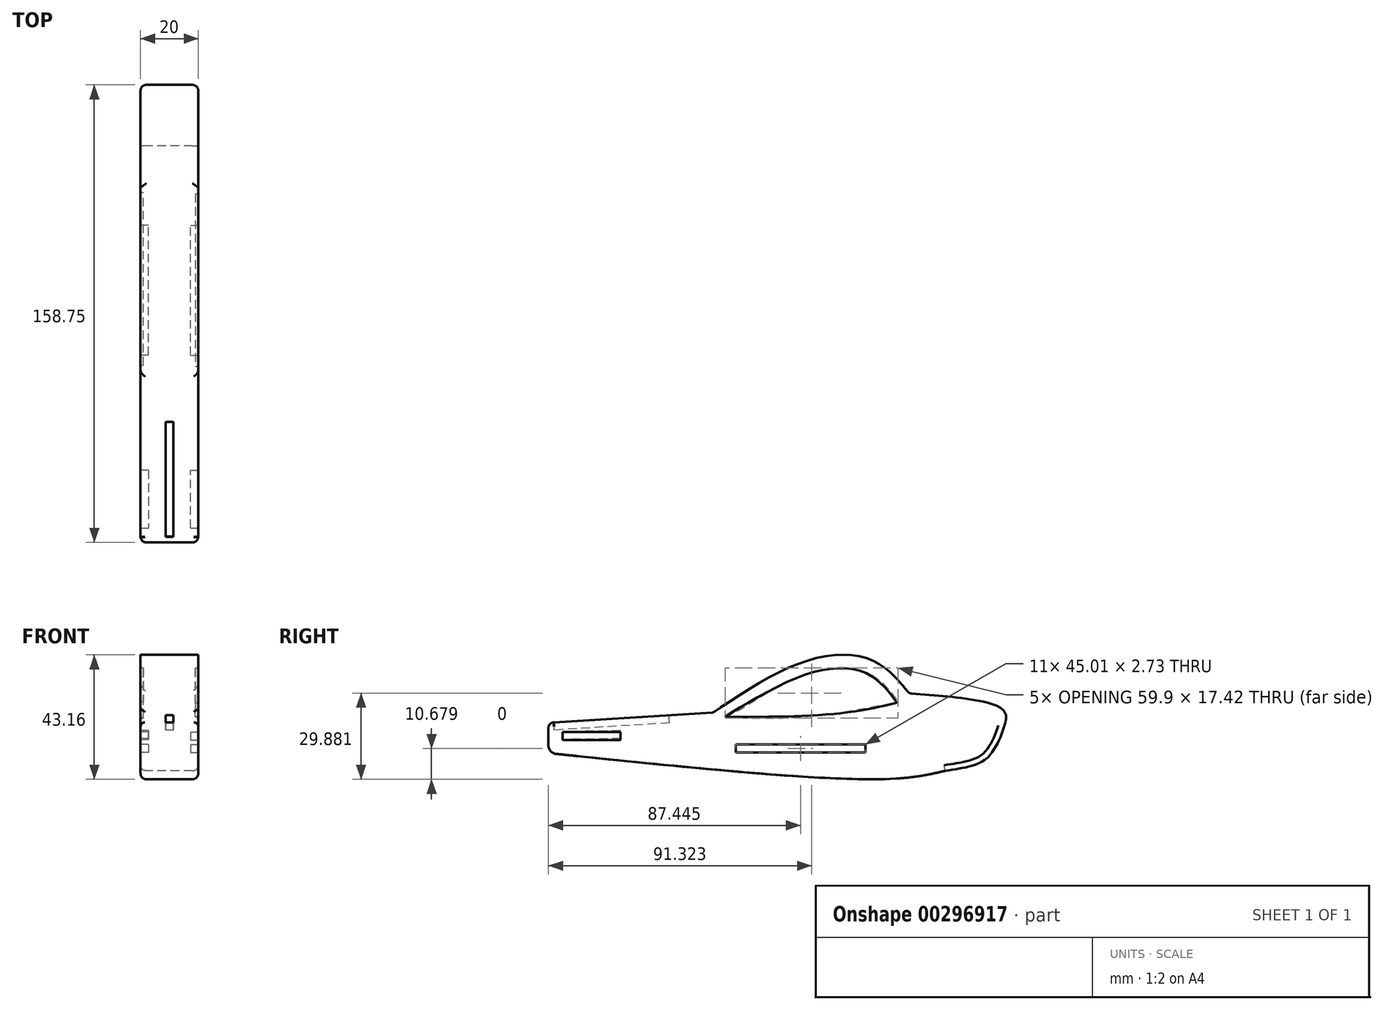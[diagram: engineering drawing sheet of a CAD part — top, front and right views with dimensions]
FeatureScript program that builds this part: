
annotation { "Feature Type Name" : "Feature", "Feature Type Description" : "" }
export const myFeature = defineFeature(function(context is Context, id is Id, definition is map)
    precondition{}
    {
        {
            var Q0;
            Q0=qCreatedBy(makeId("Right.planeOp"),FACE);
            var sketch = newSketch(context, id + "F0", { "sketchPlane" : qUnion([Q0])});
            skPoint(sketch, "E0.MirrorCS.end.orphan", {"position": v(-80.31, 27.96) * mm});
            skPoint(sketch, "E0.MirrorCS.start.orphan", {"position": v(0, 27.96) * mm});
            skFitSpline(sketch, "E1", {"points": [v(80.31, 27.96) * mm, v(77.68, 15.16) * mm, v(74.67, 8.15) * mm, v(70, 3.14) * mm, v(57.32, 0) * mm], "startDerivative": vector(-8.17, -48.04) * mm, "endDerivative": vector(-50.28, -7.34) * mm});
            skFitSpline(sketch, "E2", {"points": [v(57.32, 0) * mm, v(36.63, -2.86) * mm, v(-80.31, 6.15) * mm], "startDerivative": vector(-55.4, -12.98) * mm, "endDerivative": vector(-200.25, 20.71) * mm});
            skPoint(sketch, "E3.orphan", {"position": v(0, 0) * mm});
            skPoint(sketch, "E4.MirrorCS.end.orphan", {"position": v(-80.31, 0) * mm});
            skLineSegment(sketch, "E5", {"start": v(51.84, -1.28) * mm, "end": v(8, -2.01) * mm});
            skLineSegment(sketch, "E6", {"start": v(-80.31, 8.85) * mm, "end": v(-80.31, 11.6) * mm});
            skPoint(sketch, "E7.end.orphan", {"position": v(0, 13.98) * mm});
            skLineSegment(sketch, "E8", {"start": v(-80.31, 11.6) * mm, "end": v(-80.31, 16.7) * mm});
            skLineSegment(sketch, "E9", {"start": v(-80.31, 16.7) * mm, "end": v(-23.08, 20.27) * mm});
            skArc(sketch, "E10.filletArc", {"start": v(-80.31, 8.85) * mm, "mid": v(-79.54, 6.84) * mm, "end": v(-77.62, 5.87) * mm});
            skFitSpline(sketch, "E11", {"points": [v(77.68, 15.16) * mm, v(77.68, 20.82) * mm, v(44.76, 26.9) * mm], "startDerivative": vector(6.77, 21) * mm, "endDerivative": vector(-62.9, 4.73) * mm});
            skFitSpline(sketch, "E12", {"points": [v(44.76, 26.9) * mm, v(41.39, 30.94) * mm, v(31.93, 38.37) * mm, v(9.99, 38.37) * mm, v(-23.08, 20.27) * mm], "startDerivative": vector(-21.38, 26.71) * mm, "endDerivative": vector(-90.44, -60.27) * mm});
            skFitSpline(sketch, "E13", {"points": [v(44.76, 26.9) * mm, v(30.29, 22.55) * mm, v(-23.08, 20.27) * mm], "startDerivative": vector(-34.74, -14.07) * mm, "endDerivative": vector(-94.83, -0.55) * mm});
            skSolve(sketch);
        }
        {
            var Q0;
            Q0 = qSketchRegion(id + "F0", true);
            extrude(context, id + "F1", {"entities" : qUnion([Q0]), "depth" : 20 * mm});
        }
        {
            var Q0;
            Q0=makeQuery(id+"F1.opExtrude","SWEPT_FACE",FACE,{"disambiguationData":[OSD([sQuery(id+"F0.wireOp",EDGE,"E11")])]});
            fillet(context, id + "F2", {"entities" : qUnion([Q0]), "radius" : 2 * mm, "tangentPropagation" : true, "allowEdgeOverflow" : false});
        }
        {
            var Q0;
            Q0=makeQuery(id+"F1.opExtrude","SWEPT_FACE",FACE,{"disambiguationData":[OSD([sQuery(id+"F0.wireOp",EDGE,"E6"),sQuery(id+"F0.wireOp",EDGE,"E8")])]});
            fillet(context, id + "F3", {"entities" : qUnion([Q0]), "radius" : 2 * mm, "tangentPropagation" : true, "allowEdgeOverflow" : false});
        }
        {
            var Q0;
            Q0=makeQuery(id+"F1.opExtrude","SWEPT_FACE",FACE,{"disambiguationData":[OSD([sQuery(id+"F0.wireOp",EDGE,"E9")])]});
            fillet(context, id + "F4", {"entities" : qUnion([Q0]), "radius" : 1.5 * mm, "tangentPropagation" : true, "allowEdgeOverflow" : false});
        }
        {
            var Q0;
            Q0=makeQuery(id+"F1.opExtrude","CAP_FACE",FACE,{"disambiguationData":[OSD([sQuery(id+"F0.wireOp",EDGE,"E1"),sQuery(id+"F0.wireOp",EDGE,"E2"),sQuery(id+"F0.wireOp",EDGE,"E5"),sQuery(id+"F0.wireOp",EDGE,"E2"),sQuery(id+"F0.wireOp",EDGE,"E6"),sQuery(id+"F0.wireOp",EDGE,"E8"),sQuery(id+"F0.wireOp",EDGE,"E9"),sQuery(id+"F0.wireOp",EDGE,"E10.filletArc"),sQuery(id+"F0.wireOp",EDGE,"E11"),sQuery(id+"F0.wireOp",EDGE,"E12")])],"isStart":true});
            var sketch = newSketch(context, id + "F5", { "sketchPlane" : qUnion([Q0])});
            skFitSpline(sketch, "E14", {"points": [v(23.32, 18.75) * mm, v(-8.3, 18.75) * mm, v(-45.48, 24.83) * mm], "startDerivative": vector(-64.91, -2.79) * mm, "endDerivative": vector(-72.58, 14.7) * mm});
            skFitSpline(sketch, "E15", {"points": [v(18.93, 18.57) * mm, v(10.2, 23.49) * mm, v(-1.4, 30.34) * mm, v(-13.98, 34.7) * mm, v(-24.14, 35.54) * mm, v(-33.83, 31.98) * mm, v(-40.96, 23.92) * mm], "startDerivative": vector(-54.18, 28.65) * mm, "endDerivative": vector(-39.46, -54.49) * mm});
            skPoint(sketch, "E16.end.orphan", {"position": v(18.93, 18.75) * mm});
            skSolve(sketch);
        }
        {
            var Q0;
            Q0 = qSketchRegion(id + "F5", true);
            extrude(context, id + "F6", {"entities" : qUnion([Q0]), "operationType" : NewBodyOperationType.REMOVE, "oppositeDirection" : true, "depth" : 1 * mm});
        }
        {
            var Q0;
            Q0=makeQuery(id+"F1.opExtrude","SWEPT_FACE",FACE,{"disambiguationData":[OSD([sQuery(id+"F0.wireOp",EDGE,"E9")])]});
            var sketch = newSketch(context, id + "F7", { "sketchPlane" : qUnion([Q0])});
            skLineSegment(sketch, "E17", {"start": v(10, -37.23) * mm, "end": v(11.34, -37.23) * mm});
            skLineSegment(sketch, "E18", {"start": v(11.34, -37.23) * mm, "end": v(11.34, -77.24) * mm});
            skPoint(sketch, "E18.endSnap0", {"position": v(18, -77.7) * mm});
            skLineSegment(sketch, "E19.MirrorCS", {"start": v(8.66, -37.23) * mm, "end": v(8.66, -77.24) * mm});
            skPoint(sketch, "E20.start.orphan", {"position": v(10, -77.24) * mm});
            skLineSegment(sketch, "E21", {"start": v(8.66, -77.24) * mm, "end": v(11.34, -77.24) * mm});
            skPoint(sketch, "E22.orphan", {"position": v(8.66, -77.7) * mm});
            skPoint(sketch, "E23.orphan", {"position": v(11.34, -77.7) * mm});
            skLineSegment(sketch, "E24", {"start": v(10, -37.23) * mm, "end": v(8.66, -37.23) * mm});
            skSolve(sketch);
        }
        {
            var Q0;
            Q0=makeQuery(id+"F7.imprint","IMPRINT",FACE,{"disambiguationData":[TD([[makeQuery(id+"F7.imprint","IMPRINT",EDGE,{"derivedFrom":sQuery(id+"F7.wireOp",EDGE,"E17")}),-1.0]])]});
            extrude(context, id + "F8", {"entities" : qUnion([Q0]), "operationType" : NewBodyOperationType.REMOVE, "oppositeDirection" : true, "depth" : 2.7 * mm});
        }
        {
            var Q0;
            Q0=makeQuery(id+"F1.opExtrude","CAP_FACE",FACE,{"disambiguationData":[OSD([sQuery(id+"F0.wireOp",EDGE,"E1"),sQuery(id+"F0.wireOp",EDGE,"E2"),sQuery(id+"F0.wireOp",EDGE,"E5"),sQuery(id+"F0.wireOp",EDGE,"E2"),sQuery(id+"F0.wireOp",EDGE,"E6"),sQuery(id+"F0.wireOp",EDGE,"E8"),sQuery(id+"F0.wireOp",EDGE,"E9"),sQuery(id+"F0.wireOp",EDGE,"E10.filletArc"),sQuery(id+"F0.wireOp",EDGE,"E11"),sQuery(id+"F0.wireOp",EDGE,"E12")])],"isStart":true});
            var sketch = newSketch(context, id + "F9", { "sketchPlane" : qUnion([Q0])});
            skLineSegment(sketch, "E25", {"start": v(0, 9.15) * mm, "end": v(-29.64, 9.15) * mm});
            skLineSegment(sketch, "E26", {"start": v(0, 9.15) * mm, "end": v(15.38, 9.15) * mm});
            skLineSegment(sketch, "E27", {"start": v(15.38, 6.4) * mm, "end": v(-29.64, 6.4) * mm});
            skPoint(sketch, "E28.start.orphan", {"position": v(0, 0) * mm});
            skPoint(sketch, "E29.end.orphan", {"position": v(-39.95, 6.4) * mm});
            skPoint(sketch, "E30.orphan", {"position": v(-39.95, 9.15) * mm});
            skLineSegment(sketch, "E31", {"start": v(-29.64, 9.15) * mm, "end": v(-29.64, 6.4) * mm});
            skPoint(sketch, "E32.orphan", {"position": v(-34.69, 7.78) * mm});
            skPoint(sketch, "E33.end.orphan", {"position": v(-29.64, 8.49) * mm});
            skPoint(sketch, "E34.orphan", {"position": v(-34.69, 9.15) * mm});
            skPoint(sketch, "E35.end.orphan", {"position": v(20.29, 8.53) * mm});
            skPoint(sketch, "E36.orphan", {"position": v(25.34, 7.78) * mm});
            skPoint(sketch, "E37.orphan", {"position": v(25.34, 6.4) * mm});
            skPoint(sketch, "E38.start.orphan", {"position": v(25.34, 9.15) * mm});
            skLineSegment(sketch, "E39", {"start": v(20.6, 6.4) * mm, "end": v(20.29, 6.4) * mm});
            skLineSegment(sketch, "E40", {"start": v(15.38, 6.4) * mm, "end": v(15.38, 9.15) * mm});
            skPoint(sketch, "E41.start.orphan", {"position": v(20.29, 9.15) * mm});
            skPoint(sketch, "E42.start.orphan", {"position": v(-29.64, 2.8) * mm});
            skPoint(sketch, "E43.start.orphan", {"position": v(-29.64, 7.78) * mm});
            skSolve(sketch);
        }
        {
            var Q0;
            Q0 = qSketchRegion(id + "F9", true);
            extrude(context, id + "F10", {"entities" : qUnion([Q0]), "operationType" : NewBodyOperationType.REMOVE, "oppositeDirection" : true, "depth" : 2.7 * mm});
        }
        {
            var Q0;
            Q0=makeQuery(id+"F1.opExtrude","CAP_FACE",FACE,{"disambiguationData":[OSD([sQuery(id+"F0.wireOp",EDGE,"E1"),sQuery(id+"F0.wireOp",EDGE,"E2"),sQuery(id+"F0.wireOp",EDGE,"E5"),sQuery(id+"F0.wireOp",EDGE,"E2"),sQuery(id+"F0.wireOp",EDGE,"E6"),sQuery(id+"F0.wireOp",EDGE,"E8"),sQuery(id+"F0.wireOp",EDGE,"E9"),sQuery(id+"F0.wireOp",EDGE,"E10.filletArc"),sQuery(id+"F0.wireOp",EDGE,"E11"),sQuery(id+"F0.wireOp",EDGE,"E12")])],"isStart":true});
            var sketch = newSketch(context, id + "F11", { "sketchPlane" : qUnion([Q0])});
            skLineSegment(sketch, "E44", {"start": v(15.38, 9.15) * mm, "end": v(15.38, 18.43) * mm});
            skPoint(sketch, "E45.start.orphan", {"position": v(78.31, 12.09) * mm});
            skPoint(sketch, "E46.end.orphan", {"position": v(15.38, 13.8) * mm});
            skLineSegment(sketch, "E47", {"start": v(78.31, 12.09) * mm, "end": v(78.28, 12.09) * mm});
            skLineSegment(sketch, "E48", {"start": v(55.3, 12.6) * mm, "end": v(55.32, 13.95) * mm});
            skLineSegment(sketch, "E49", {"start": v(55.32, 13.95) * mm, "end": v(75.26, 13.51) * mm});
            skLineSegment(sketch, "E50.MirrorCS", {"start": v(55.26, 11.24) * mm, "end": v(75.26, 10.8) * mm});
            skLineSegment(sketch, "E51.MirrorCS", {"start": v(55.3, 12.6) * mm, "end": v(55.26, 11.24) * mm});
            skLineSegment(sketch, "E52", {"start": v(78.25, 10.73) * mm, "end": v(78.31, 10.73) * mm});
            skPoint(sketch, "E53.orphan", {"position": v(75.26, 12.16) * mm});
            skPoint(sketch, "E54.start.orphan", {"position": v(78.31, 13.45) * mm});
            skLineSegment(sketch, "E55", {"start": v(75.26, 13.51) * mm, "end": v(75.43, 13.5) * mm});
            skLineSegment(sketch, "E56", {"start": v(75.43, 13.5) * mm, "end": v(75.43, 10.8) * mm});
            skLineSegment(sketch, "E57", {"start": v(75.26, 10.8) * mm, "end": v(75.43, 10.8) * mm});
            skSolve(sketch);
        }
        {
            var Q0;
            Q0 = qSketchRegion(id + "F11", true);
            extrude(context, id + "F12", {"entities" : qUnion([Q0]), "operationType" : NewBodyOperationType.REMOVE, "oppositeDirection" : true, "depth" : 2.7 * mm});
        }
        {
            var Q0;
            Q0=makeQuery(id+"F1.opExtrude","CAP_FACE",FACE,{"disambiguationData":[OSD([sQuery(id+"F0.wireOp",EDGE,"E1"),sQuery(id+"F0.wireOp",EDGE,"E2"),sQuery(id+"F0.wireOp",EDGE,"E5"),sQuery(id+"F0.wireOp",EDGE,"E2"),sQuery(id+"F0.wireOp",EDGE,"E6"),sQuery(id+"F0.wireOp",EDGE,"E8"),sQuery(id+"F0.wireOp",EDGE,"E9"),sQuery(id+"F0.wireOp",EDGE,"E10.filletArc"),sQuery(id+"F0.wireOp",EDGE,"E11"),sQuery(id+"F0.wireOp",EDGE,"E12")])],"isStart":false});
            var sketch = newSketch(context, id + "F13", { "sketchPlane" : qUnion([Q0])});
            skLineSegment(sketch, "E58", {"start": v(-55.27, 12.09) * mm, "end": v(-55.27, 13.44) * mm});
            skLineSegment(sketch, "E59", {"start": v(-75.33, 13.44) * mm, "end": v(-55.27, 13.44) * mm});
            skLineSegment(sketch, "E60.MirrorCS", {"start": v(-75.33, 10.74) * mm, "end": v(-55.27, 10.74) * mm});
            skLineSegment(sketch, "E61", {"start": v(-55.27, 12.09) * mm, "end": v(-55.27, 10.74) * mm});
            skLineSegment(sketch, "E62", {"start": v(-75.33, 10.74) * mm, "end": v(-75.33, 13.44) * mm});
            skPoint(sketch, "E63.start.orphan", {"position": v(-78.31, 12.09) * mm});
            skPoint(sketch, "E64.end.orphan", {"position": v(-75.33, 12.09) * mm});
            skSolve(sketch);
        }
        {
            var Q0;
            Q0 = qSketchRegion(id + "F13", true);
            extrude(context, id + "F14", {"entities" : qUnion([Q0]), "operationType" : NewBodyOperationType.REMOVE, "oppositeDirection" : true, "depth" : 2.7 * mm});
        }
        {
            var Q0;
            Q0=makeQuery(id+"F1.opExtrude","CAP_FACE",FACE,{"disambiguationData":[OSD([sQuery(id+"F0.wireOp",EDGE,"E1"),sQuery(id+"F0.wireOp",EDGE,"E2"),sQuery(id+"F0.wireOp",EDGE,"E5"),sQuery(id+"F0.wireOp",EDGE,"E2"),sQuery(id+"F0.wireOp",EDGE,"E6"),sQuery(id+"F0.wireOp",EDGE,"E8"),sQuery(id+"F0.wireOp",EDGE,"E9"),sQuery(id+"F0.wireOp",EDGE,"E10.filletArc"),sQuery(id+"F0.wireOp",EDGE,"E11"),sQuery(id+"F0.wireOp",EDGE,"E12")])],"isStart":false});
            var sketch = newSketch(context, id + "F15", { "sketchPlane" : qUnion([Q0])});
            skLineSegment(sketch, "E65", {"start": v(0, 9.11) * mm, "end": v(-15.37, 9.11) * mm});
            skLineSegment(sketch, "E66", {"start": v(0, 9.11) * mm, "end": v(29.64, 9.11) * mm});
            skLineSegment(sketch, "E67", {"start": v(-15.37, 9.11) * mm, "end": v(-15.37, 6.38) * mm});
            skLineSegment(sketch, "E68", {"start": v(-15.37, 6.38) * mm, "end": v(29.64, 6.38) * mm});
            skLineSegment(sketch, "E69", {"start": v(29.64, 6.38) * mm, "end": v(29.64, 9.11) * mm});
            skSolve(sketch);
        }
        {
            var Q0;
            Q0 = qSketchRegion(id + "F15", true);
            extrude(context, id + "F16", {"entities" : qUnion([Q0]), "operationType" : NewBodyOperationType.REMOVE, "oppositeDirection" : true, "depth" : 2.7 * mm});
        }
        {
            var Q0;
            Q0=makeQuery(id+"F1.opExtrude","CAP_FACE",FACE,{"disambiguationData":[OSD([sQuery(id+"F0.wireOp",EDGE,"E1"),sQuery(id+"F0.wireOp",EDGE,"E2"),sQuery(id+"F0.wireOp",EDGE,"E5"),sQuery(id+"F0.wireOp",EDGE,"E2"),sQuery(id+"F0.wireOp",EDGE,"E6"),sQuery(id+"F0.wireOp",EDGE,"E8"),sQuery(id+"F0.wireOp",EDGE,"E9"),sQuery(id+"F0.wireOp",EDGE,"E10.filletArc"),sQuery(id+"F0.wireOp",EDGE,"E11"),sQuery(id+"F0.wireOp",EDGE,"E12")])],"isStart":false});
            var sketch = newSketch(context, id + "F17", { "sketchPlane" : qUnion([Q0])});
            skFitSpline(sketch, "E70", {"points": [v(45.48, 24.83) * mm, v(21.06, 19.99) * mm, v(-23.32, 18.75) * mm], "startDerivative": vector(-52.62, -13.27) * mm, "endDerivative": vector(-83.5, 0.45) * mm});
            skFitSpline(sketch, "E71", {"points": [v(-19.17, 18.73) * mm, v(-8.9, 24.83) * mm, v(5.72, 32.23) * mm, v(16.09, 35.2) * mm, v(24, 35.47) * mm, v(30.92, 33.44) * mm, v(37.6, 27.63) * mm, v(40.59, 23.61) * mm], "startDerivative": vector(60, 35.92) * mm, "endDerivative": vector(24.53, -36.05) * mm});
            skSolve(sketch);
        }
        {
            var Q0;
            Q0 = qSketchRegion(id + "F17", true);
            extrude(context, id + "F18", {"entities" : qUnion([Q0]), "operationType" : NewBodyOperationType.REMOVE, "oppositeDirection" : true, "depth" : 1 * mm});
        }
    });
